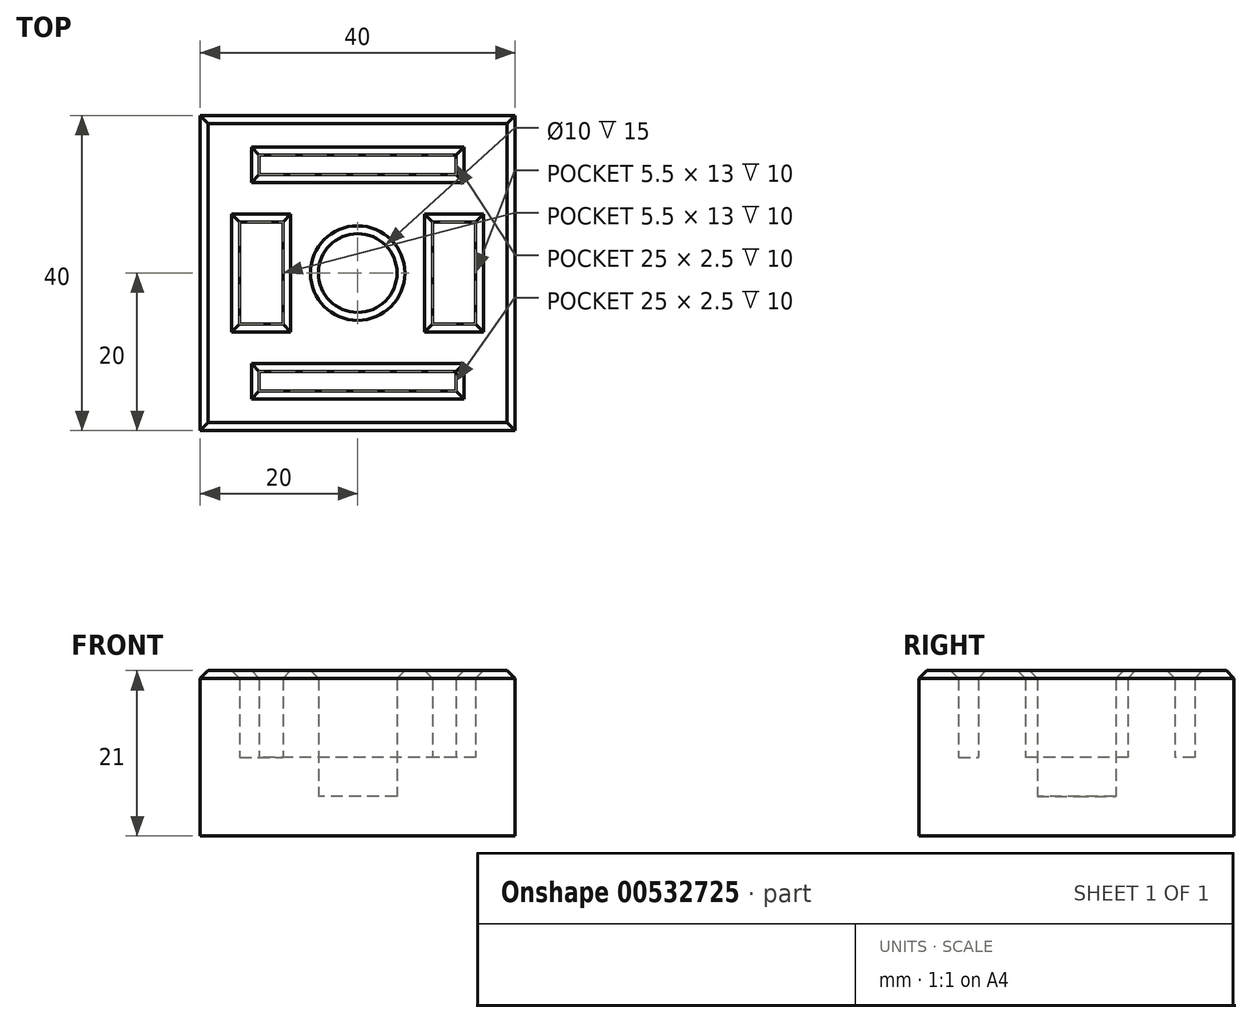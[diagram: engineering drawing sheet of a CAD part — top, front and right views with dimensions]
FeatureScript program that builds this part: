
annotation { "Feature Type Name" : "Feature", "Feature Type Description" : "" }
export const myFeature = defineFeature(function(context is Context, id is Id, definition is map)
    precondition{}
    {
        {
            var Q0;
            Q0=qCreatedBy(makeId("Top.planeOp"),FACE);
            var sketch = newSketch(context, id + "F0", { "sketchPlane" : qUnion([Q0])});
            skLineSegment(sketch, "E0.bottom", {"start": v(20, 20) * mm, "end": v(-20, 20) * mm});
            skLineSegment(sketch, "E0.top", {"start": v(20, -20) * mm, "end": v(-20, -20) * mm});
            skLineSegment(sketch, "E0.left", {"start": v(20, 20) * mm, "end": v(20, -20) * mm});
            skLineSegment(sketch, "E0.right", {"start": v(-20, 20) * mm, "end": v(-20, -20) * mm});
            skPoint(sketch, "E0.middle", {"position": v(0, 0) * mm});
            skSolve(sketch);
        }
        {
            var Q0;
            Q0 = qSketchRegion(id + "F0", true);
            extrude(context, id + "F1", {"entities" : qUnion([Q0]), "depth" : 10 * mm, "offsetDistance" : 25 * mm});
        }
        {
            var Q0;
            Q0=makeQuery(id+"F1.opExtrude","CAP_FACE",FACE,{"disambiguationData":[OSD([sQuery(id+"F0.wireOp",EDGE,"E0.bottom"),sQuery(id+"F0.wireOp",EDGE,"E0.top"),sQuery(id+"F0.wireOp",EDGE,"E0.left"),sQuery(id+"F0.wireOp",EDGE,"E0.right")])],"isStart":false});
            var sketch = newSketch(context, id + "F2", { "sketchPlane" : qUnion([Q0])});
            skCircle(sketch, "E1", {"center": v(0, 0) * mm, "radius": 5 * mm});
            skLineSegment(sketch, "E2.bottom", {"start": v(15, 6.5) * mm, "end": v(9.5, 6.5) * mm});
            skLineSegment(sketch, "E2.top", {"start": v(15, -6.5) * mm, "end": v(9.5, -6.5) * mm});
            skLineSegment(sketch, "E2.left", {"start": v(15, 6.5) * mm, "end": v(15, -6.5) * mm});
            skLineSegment(sketch, "E2.right", {"start": v(9.5, 6.5) * mm, "end": v(9.5, -6.5) * mm});
            skPoint(sketch, "E2.middle", {"position": v(12.25, 0) * mm});
            skLineSegment(sketch, "E3.MirrorCS", {"start": v(-9.5, 6.5) * mm, "end": v(-9.5, -6.5) * mm});
            skLineSegment(sketch, "E4.MirrorCS", {"start": v(-15, 6.5) * mm, "end": v(-9.5, 6.5) * mm});
            skLineSegment(sketch, "E5.MirrorCS", {"start": v(-15, 6.5) * mm, "end": v(-15, -6.5) * mm});
            skLineSegment(sketch, "E6.MirrorCS", {"start": v(-15, -6.5) * mm, "end": v(-9.5, -6.5) * mm});
            skLineSegment(sketch, "E7.bottom", {"start": v(12.5, 15) * mm, "end": v(-12.5, 15) * mm});
            skLineSegment(sketch, "E7.top", {"start": v(12.5, 12.5) * mm, "end": v(-12.5, 12.5) * mm});
            skLineSegment(sketch, "E7.left", {"start": v(12.5, 15) * mm, "end": v(12.5, 12.5) * mm});
            skLineSegment(sketch, "E7.right", {"start": v(-12.5, 15) * mm, "end": v(-12.5, 12.5) * mm});
            skPoint(sketch, "E7.middle", {"position": v(0, 13.75) * mm});
            skLineSegment(sketch, "E8.MirrorCS", {"start": v(12.5, -12.5) * mm, "end": v(-12.5, -12.5) * mm});
            skLineSegment(sketch, "E9.MirrorCS", {"start": v(-12.5, -15) * mm, "end": v(-12.5, -12.5) * mm});
            skLineSegment(sketch, "E10.MirrorCS", {"start": v(12.5, -15) * mm, "end": v(-12.5, -15) * mm});
            skLineSegment(sketch, "E11.MirrorCS", {"start": v(12.5, -15) * mm, "end": v(12.5, -12.5) * mm});
            skSolve(sketch);
        }
        {
            var Q0;
            Q0=makeQuery(id+"F2.imprint","IMPRINT",FACE,{"disambiguationData":[TD([[makeQuery(id+"F2.imprint","IMPRINT",EDGE,{"derivedFrom":sQuery(id+"F2.wireOp",EDGE,"E1")}),-1.0]])]});
            extrude(context, id + "F3", {"entities" : qUnion([Q0]), "operationType" : NewBodyOperationType.ADD, "depth" : 11 * mm, "offsetDistance" : 25 * mm});
        }
        {
            var Q0;
            Q0=makeQuery(id+"F3.boolean.opBoolean","SPLIT",FACE,{"disambiguationData":[TD([makeQuery(id+"F3.opExtrude","SWEPT_FACE",FACE,{"disambiguationData":[OSD([sQuery(id+"F2.wireOp",EDGE,"E1")])]})])],"derivedFrom":makeQuery(id+"F1.opExtrude","CAP_FACE",FACE,{"disambiguationData":[OSD([sQuery(id+"F0.wireOp",EDGE,"E0.bottom"),sQuery(id+"F0.wireOp",EDGE,"E0.top"),sQuery(id+"F0.wireOp",EDGE,"E0.left"),sQuery(id+"F0.wireOp",EDGE,"E0.right")])],"isStart":false})});
            extrude(context, id + "F4", {"entities" : qUnion([Q0]), "operationType" : NewBodyOperationType.REMOVE, "oppositeDirection" : true, "depth" : 5 * mm, "offsetDistance" : 25 * mm});
        }
        {
            var Q0;
            Q0=makeQuery(id+"F3.opExtrude","CAP_FACE",FACE,{"disambiguationData":[OSD([sQuery(id+"F0.wireOp",EDGE,"E0.bottom"),sQuery(id+"F0.wireOp",EDGE,"E0.top"),sQuery(id+"F0.wireOp",EDGE,"E0.left"),sQuery(id+"F0.wireOp",EDGE,"E0.right"),sQuery(id+"F2.wireOp",EDGE,"E1"),sQuery(id+"F2.wireOp",EDGE,"E2.bottom"),sQuery(id+"F2.wireOp",EDGE,"E2.top"),sQuery(id+"F2.wireOp",EDGE,"E2.left"),sQuery(id+"F2.wireOp",EDGE,"E2.right"),sQuery(id+"F2.wireOp",EDGE,"E3.MirrorCS"),sQuery(id+"F2.wireOp",EDGE,"E4.MirrorCS"),sQuery(id+"F2.wireOp",EDGE,"E5.MirrorCS"),sQuery(id+"F2.wireOp",EDGE,"E6.MirrorCS"),sQuery(id+"F2.wireOp",EDGE,"E7.bottom"),sQuery(id+"F2.wireOp",EDGE,"E7.top"),sQuery(id+"F2.wireOp",EDGE,"E7.left"),sQuery(id+"F2.wireOp",EDGE,"E7.right"),sQuery(id+"F2.wireOp",EDGE,"E8.MirrorCS"),sQuery(id+"F2.wireOp",EDGE,"E9.MirrorCS"),sQuery(id+"F2.wireOp",EDGE,"E10.MirrorCS"),sQuery(id+"F2.wireOp",EDGE,"E11.MirrorCS")])],"isStart":false});
            chamfer(context, id + "F5", {"entities" : qUnion([Q0]), "width" : 1 * mm, "tangentPropagation" : true});
        }
    });
